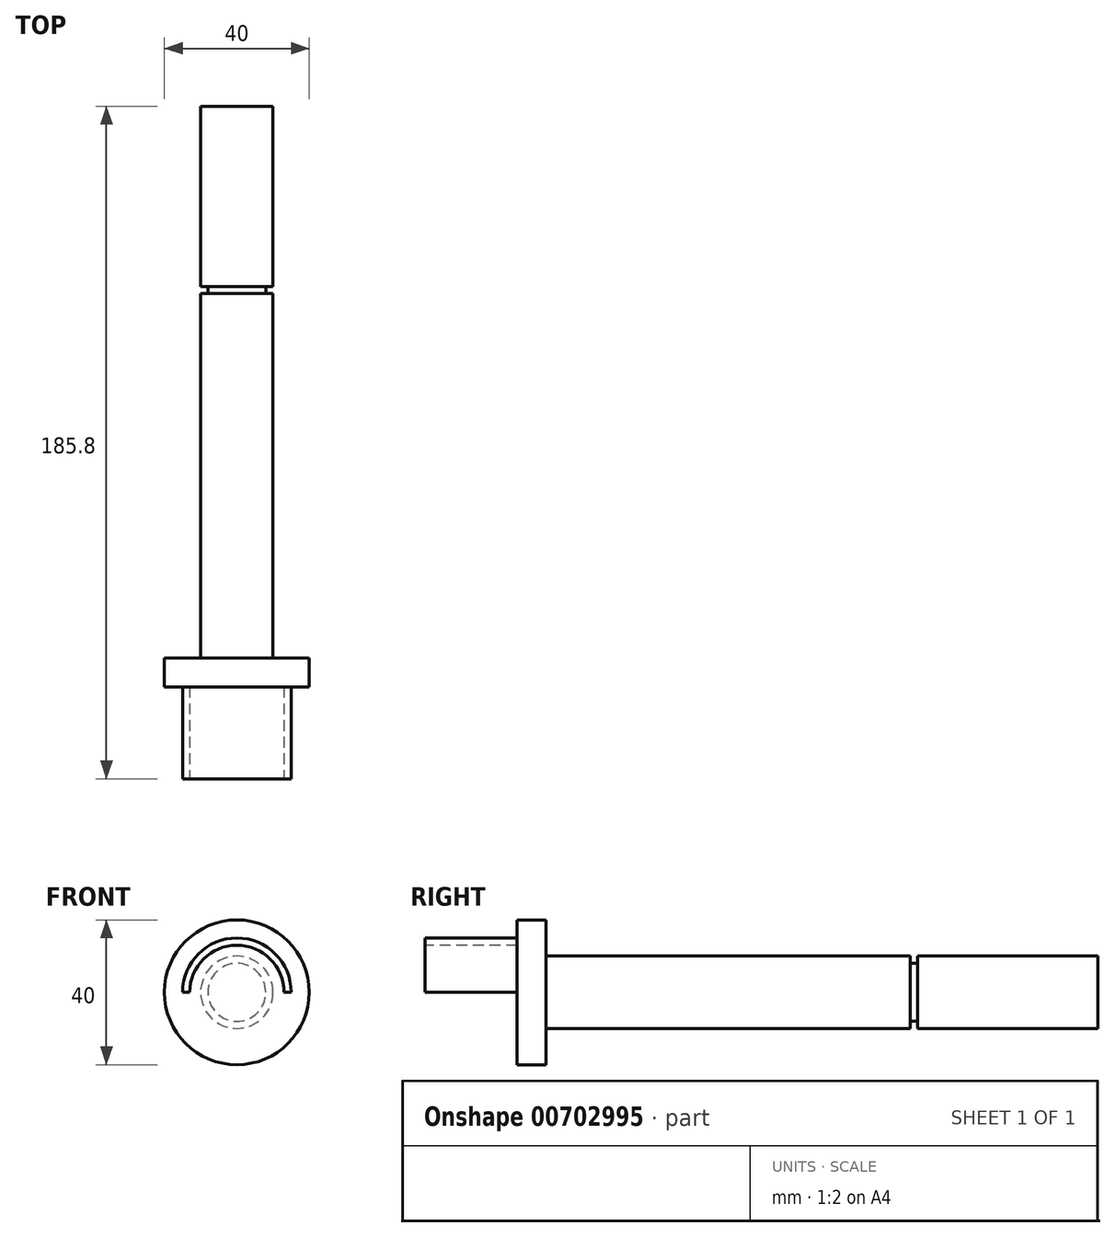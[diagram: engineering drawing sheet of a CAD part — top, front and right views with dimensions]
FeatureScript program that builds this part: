
annotation { "Feature Type Name" : "Feature", "Feature Type Description" : "" }
export const myFeature = defineFeature(function(context is Context, id is Id, definition is map)
    precondition{}
    {
        {
            var Q0;
            Q0=qCreatedBy(makeId("Front.planeOp"),FACE);
            var sketch = newSketch(context, id + "F0", { "sketchPlane" : qUnion([Q0])});
            skCircle(sketch, "E0", {"center": v(0, 0) * mm, "radius": 15 * mm});
            skCircle(sketch, "E1", {"center": v(0, 0) * mm, "radius": 13 * mm});
            skLineSegment(sketch, "E2.bottom", {"start": v(15, 15) * mm, "end": v(-15, 15) * mm});
            skLineSegment(sketch, "E2.top", {"start": v(15, 0) * mm, "end": v(-15, 0) * mm});
            skLineSegment(sketch, "E2.left", {"start": v(15, 15) * mm, "end": v(15, 0) * mm});
            skLineSegment(sketch, "E2.right", {"start": v(-15, 15) * mm, "end": v(-15, 0) * mm});
            skSolve(sketch);
        }
        {
            var Q0;
            {var subQ0=sQuery(id+"F0.wireOp",EDGE,"E2.top");var subQ4=sQuery(id+"F0.wireOp",EDGE,"E1");var subQ5=makeQuery(id+"F0.imprint","INTERSECT",VERTEX,{"disambiguationData":[OD(0.0)],"derivedFrom":[subQ4,subQ0]});Q0=makeQuery(id+"F0.imprint","IMPRINT",FACE,{"disambiguationData":[TD([[makeQuery(id+"F0.imprint","IMPRINT",EDGE,{"disambiguationData":[TD([[subQ5,1.0]])],"derivedFrom":subQ4}),-1.0]])]});}
            extrude(context, id + "F1", {"entities" : qUnion([Q0]), "oppositeDirection" : true, "depth" : 25.4 * mm, "offsetDistance" : 25.4 * mm});
        }
        {
            var Q0;
            Q0=makeQuery(id+"F1.opExtrude","CAP_FACE",FACE,{"disambiguationData":[OSD([sQuery(id+"F0.wireOp",EDGE,"E0"),sQuery(id+"F0.wireOp",EDGE,"E1"),sQuery(id+"F0.wireOp",EDGE,"E2.top")])],"isStart":false});
            var sketch = newSketch(context, id + "F2", { "sketchPlane" : qUnion([Q0])});
            skCircle(sketch, "E3", {"center": v(0, 0) * mm, "radius": 20 * mm});
            skSolve(sketch);
        }
        {
            var Q0;
            Q0=makeQuery(id+"F2.imprint","IMPRINT",FACE,{"disambiguationData":[TD([[makeQuery(id+"F2.imprint","IMPRINT",EDGE,{"derivedFrom":sQuery(id+"F2.wireOp",EDGE,"E3")}),1.0]])]});
            var Q1;
            {var subQ0=sQuery(id+"F0.wireOp",EDGE,"E0");Q1=makeQuery(id+"F2.imprint","IMPRINT",FACE,{"disambiguationData":[TD([[makeQuery(id+"F2.imprint","IMPRINT",EDGE,{"derivedFrom":makeQuery(id+"F1.opExtrude","CAP_EDGE",EDGE,{"disambiguationData":[OSD([subQ0])],"isStart":false})}),-1.0]])]});}
            extrude(context, id + "F3", {"entities" : qUnion([Q0, Q1]), "depth" : 8 * mm, "offsetDistance" : 25.4 * mm});
        }
        {
            var Q0;
            Q0=makeQuery(id+"F3.opExtrude","CAP_FACE",FACE,{"disambiguationData":[OSD([sQuery(id+"F2.wireOp",EDGE,"E3")])],"isStart":false});
            var sketch = newSketch(context, id + "F4", { "sketchPlane" : qUnion([Q0])});
            skCircle(sketch, "E4", {"center": v(0, 0) * mm, "radius": 10 * mm});
            skSolve(sketch);
        }
        {
            var Q0;
            Q0=makeQuery(id+"F4.imprint","IMPRINT",FACE,{"disambiguationData":[TD([[makeQuery(id+"F4.imprint","IMPRINT",EDGE,{"derivedFrom":sQuery(id+"F4.wireOp",EDGE,"E4")}),1.0]])]});
            extrude(context, id + "F5", {"entities" : qUnion([Q0]), "operationType" : NewBodyOperationType.ADD, "depth" : 152.4 * mm, "offsetDistance" : 25.4 * mm});
        }
        {
            var Q0;
            Q0=makeQuery(id+"F5.opExtrude","CAP_FACE",FACE,{"disambiguationData":[OSD([sQuery(id+"F4.wireOp",EDGE,"E4")])],"isStart":false});
            cPlane(context, id + "F6", {"entities" : qUnion([Q0]), "cplaneType" : CPlaneType.OFFSET, "offset" : 50.8 * mm, "oppositeDirection" : true, "width" : 152.4 * mm, "height" : 152.4 * mm});
        }
        {
            var Q0;
            Q0=qCreatedBy(id+"F6.planeOp",FACE);
            var sketch = newSketch(context, id + "F7", { "sketchPlane" : qUnion([Q0])});
            skCircle(sketch, "E5", {"center": v(0, 0) * mm, "radius": 12.7 * mm});
            skCircle(sketch, "E6", {"center": v(0, 0) * mm, "radius": 8 * mm});
            skSolve(sketch);
        }
        {
            var Q0;
            Q0=makeQuery(id+"F7.imprint","IMPRINT",FACE,{"disambiguationData":[TD([[makeQuery(id+"F7.imprint","IMPRINT",EDGE,{"derivedFrom":sQuery(id+"F7.wireOp",EDGE,"E5")}),1.0]])]});
            extrude(context, id + "F8", {"entities" : qUnion([Q0]), "operationType" : NewBodyOperationType.REMOVE, "endBound" : BoundingType.SYMMETRIC, "oppositeDirection" : true, "depth" : 2 * mm, "offsetDistance" : 25.4 * mm});
        }
    });
